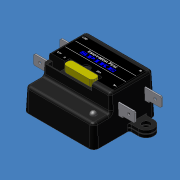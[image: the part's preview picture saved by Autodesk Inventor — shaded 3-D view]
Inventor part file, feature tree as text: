
AUTODESK INVENTOR PART (.ipt)
format: ipt  version: 2012 (Build 160160000, 160)  size: 628,224 bytes
history: native  units: mm (DEFAULTED — no unit token found)
features: sketch x19, extrude x13, projected_geometry x5, plane x4, mirror x2, revolve x1, fillet x1, other x1
ambient origin geometry x8: Origin, YZ Plane, XZ Plane, XY Plane, X Axis, Y Axis, Z Axis, Center Point
bodies: Solid1 (feature_tree)
feature tree (46):
  extrude  "Extrusion1"  Depth=41.656mm
  plane  "Work Plane1"
  extrude  "Extrusion2"  Depth=26.035mm
  extrude  "Extrusion3"  Depth=11.43mm
  plane  "Work Plane2"
  extrude  "Extrusion4"  Depth=26.035mm TaperAngle=0.0deg
  plane  "Work Plane3"
  mirror  "Mirror1"
  extrude  "Extrusion5"  Depth=10.16mm
  revolve  "Revolution1"  [1 undecoded]
  plane  "Work Plane4"
  extrude  "Extrusion6"  Depth=1.905mm TaperAngle=0.0deg
  extrude  "Extrusion7"  Depth=1.905mm TaperAngle=0.0deg
  extrude  "Extrusion8"  TaperAngle=0.0deg  [1 undecoded]
  mirror  "Mirror2"
  extrude  "Extrusion9"  Depth=21.59mm
  extrude  "Extrusion10"  Depth=3.81mm
  extrude  "Extrusion11"  Depth=0.635mm
  extrude  "Extrusion12"  Depth=3.81mm
  extrude  "Extrusion13"  Depth=23.3045mm
  fillet  "Fillet1"  Radius=0.889mm
  sketch  "Sketch16"  dims[d35=6.35mm]
  sketch  "Sketch17"  dims[d36=0.889mm]
  sketch  "Sketch18"  dims[d37=16.51mm]
  sketch  "Sketch19"  dims[d38=10.16mm d39=0.0mm d40=10.795mm d41=0.0mm d42=1.905mm d43=2.54mm d44=6.35mm d46=8.225975mm d47=4.127233mm d48=0.635mm d49=0.635mm d50=0.635mm d51=0.635mm d52=10.795mm d53=0.0mm d54=10.795mm d55=0.0mm d56=3.175mm d57=8.255mm d58=0.0mm d60=0.0mm d61=7.239mm d62=0.0mm d63=1.27mm d64=1.27mm d65=30.0mm d67=2.54mm d68=10.0mm d70=25.4mm d72=0.9525mm d73=0.9525mm d74=0.635mm d75=-6.981317mm d76=5.08mm d77=0.889mm d78=0.0mm d79=19.05mm d80=5.08mm d81=1.905mm d82=0.889mm d83=0.0mm d84=1.524mm d86=41.91mm]
  sketch  "Sketch1"  dims[d0=46.609mm d1=41.656mm]
  sketch  "Sketch2"  dims[d2=3.175mm d3=26.035mm d4=-0.523599mm]
  sketch  "Sketch3"  dims[d5=4.6355mm d6=11.43mm]
  sketch  "Sketch4"  dims[d7=11.43mm d8=26.035mm d9=0.0mm]
  projected_geometry  "Projected Loop1"
  sketch  "Sketch5"  dims[d10=5.08mm d11=10.16mm]
  sketch  "Sketch6"  dims[d12=5.969mm d13=8.001mm]
  sketch  "Sketch7"  dims[d14=1.27mm d15=1.905mm d16=0.0mm]
  projected_geometry  "Projected Loop2"
  projected_geometry  "Projected Loop3"
  sketch  "Sketch8"  dims[d17=0.508mm d18=1.905mm d19=0.0mm]
  projected_geometry  "Projected Loop4"
  sketch  "Sketch9"  dims[d20=23.3045mm d21=0.0mm]
  sketch  "Sketch10"  dims[d22=6.985mm d23=21.59mm]
  projected_geometry  "Projected Loop5"
  sketch  "Sketch11"  dims[d24=10.795mm d25=3.81mm]
  sketch  "Sketch12"  dims[d26=0.635mm d27=0.635mm]
  sketch  "Sketch13"  dims[d28=4.191mm d29=0.0mm d30=3.81mm]
  sketch  "Sketch14"  dims[d31=90.0deg d32=23.3045mm d33=0.889mm]
  sketch  "Sketch15"  dims[d34=7.366mm]
  other  "Image1"
note: 2 required parameter values undecoded (feature->parameter linkage not recoverable at this tier; creation-order binding heuristic only, values carry confidence <= 0.55)